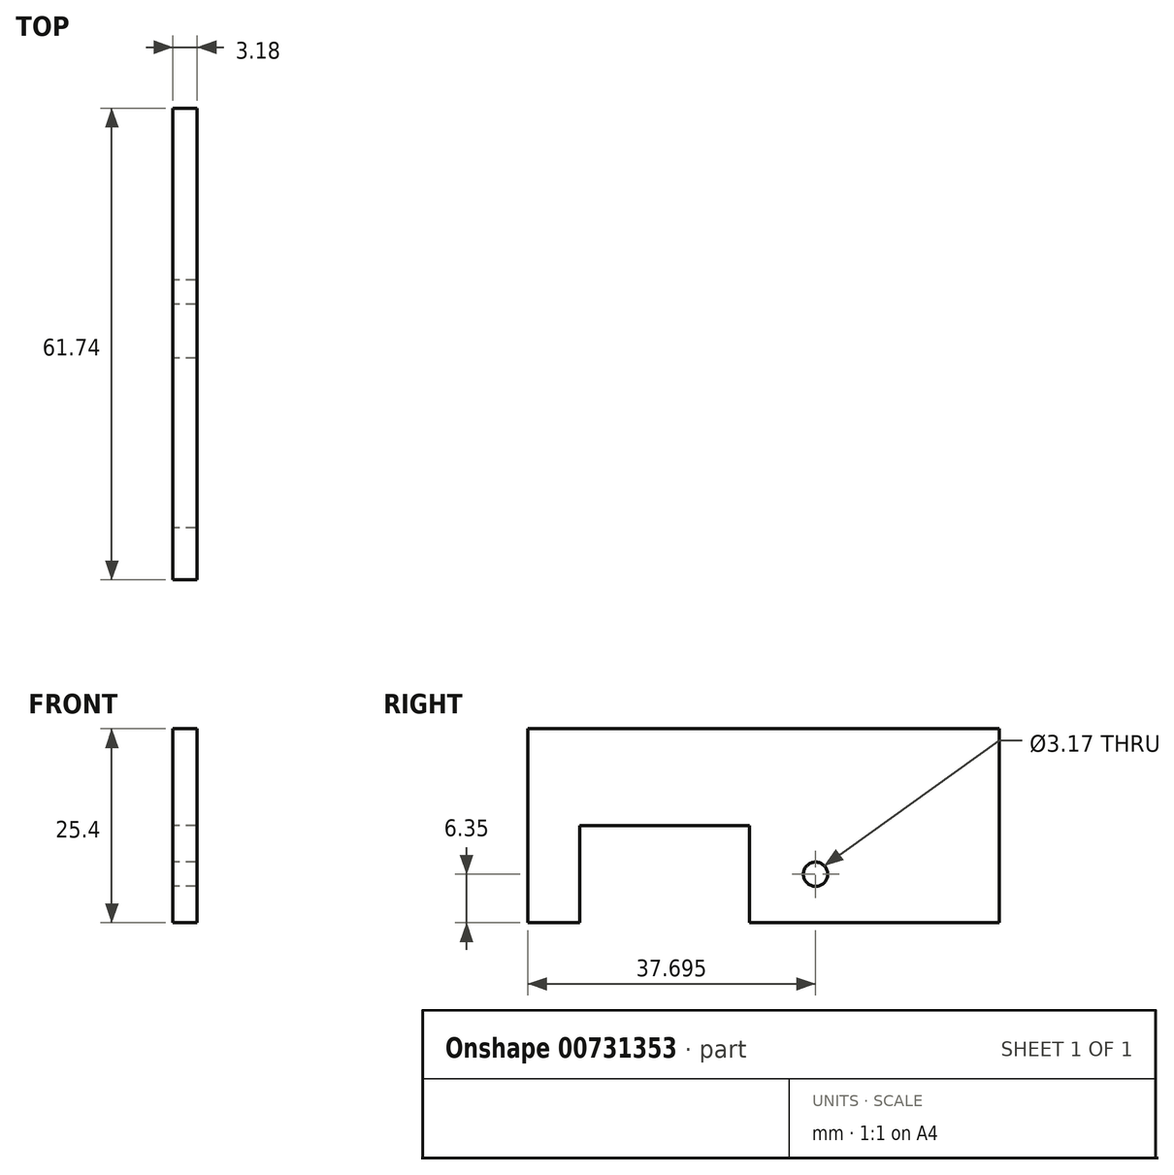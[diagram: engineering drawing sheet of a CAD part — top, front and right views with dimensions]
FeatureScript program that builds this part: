
annotation { "Feature Type Name" : "Feature", "Feature Type Description" : "" }
export const myFeature = defineFeature(function(context is Context, id is Id, definition is map)
    precondition{}
    {
        {
            var Q0;
            Q0=qCreatedBy(makeId("Right.planeOp"),FACE);
            var sketch = newSketch(context, id + "F0", { "sketchPlane" : qUnion([Q0])});
            skLineSegment(sketch, "E0.bottom", {"start": v(-30.87, 0) * mm, "end": v(30.87, 0) * mm});
            skLineSegment(sketch, "E0.top", {"start": v(-30.87, 25.4) * mm, "end": v(30.87, 25.4) * mm});
            skLineSegment(sketch, "E0.left", {"start": v(-30.87, 0) * mm, "end": v(-30.87, 25.4) * mm});
            skLineSegment(sketch, "E0.right", {"start": v(30.87, 0) * mm, "end": v(30.87, 25.4) * mm});
            skLineSegment(sketch, "E1", {"start": v(-30.87, 0) * mm, "end": v(-24.05, 0) * mm, "construction": true});
            skLineSegment(sketch, "E2", {"start": v(-24.05, 0) * mm, "end": v(-24.05, 12.7) * mm});
            skLineSegment(sketch, "E3", {"start": v(-24.05, 12.7) * mm, "end": v(-1.82, 12.7) * mm});
            skLineSegment(sketch, "E4", {"start": v(-1.82, 12.7) * mm, "end": v(-1.82, 0) * mm});
            skLineSegment(sketch, "E5", {"start": v(30.87, 0) * mm, "end": v(30.87, 6.35) * mm});
            skLineSegment(sketch, "E6", {"start": v(30.87, 6.35) * mm, "end": v(6.83, 6.35) * mm, "construction": true});
            skCircle(sketch, "E7", {"center": v(6.83, 6.35) * mm, "radius": 1.59 * mm});
            skSolve(sketch);
        }
        {
            var Q0;
            Q0=makeQuery(id+"F0.imprint","IMPRINT",FACE,{"disambiguationData":[TD([[makeQuery(id+"F0.imprint","IMPRINT",EDGE,{"derivedFrom":sQuery(id+"F0.wireOp",EDGE,"E0.top")}),-1.0]])]});
            extrude(context, id + "F1", {"entities" : qUnion([Q0]), "depth" : 3.17 * mm, "offsetDistance" : 25.4 * mm});
        }
    });
